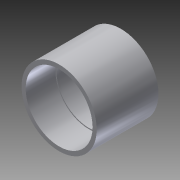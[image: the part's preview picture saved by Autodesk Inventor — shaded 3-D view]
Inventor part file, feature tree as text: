
AUTODESK INVENTOR PART (.ipt)
format: ipt  version: 2014 (Build 180170000, 170)  size: 104,960 bytes
history: native  units: in
note: dims shown in document units (in); Inventor stores cm internally (conversion verified against a paired STEP export)
features: extrude x3, sketch x3
ambient origin geometry x8: Origin, YZ Plane, XZ Plane, XY Plane, X Axis, Y Axis, Z Axis, Center Point
bodies: Solid1 (feature_tree)
feature tree (6):
  extrude  "Extrusion1"  Depth=0.1969in
  extrude  "Extrusion2"  Depth=2.3622in
  extrude  "Extrusion3"  Depth=1.1417in
  sketch  "Sketch1"  dims[d0=2.4803in d1=0.1969in]
  sketch  "Sketch3"  dims[d2=2.3622in d3=0.0in d4=2.5591in]
  sketch  "Sketch4"  dims[d5=1.1417in d6=0.0in d7=2.5591in d8=1.1417in d9=0.0in]
